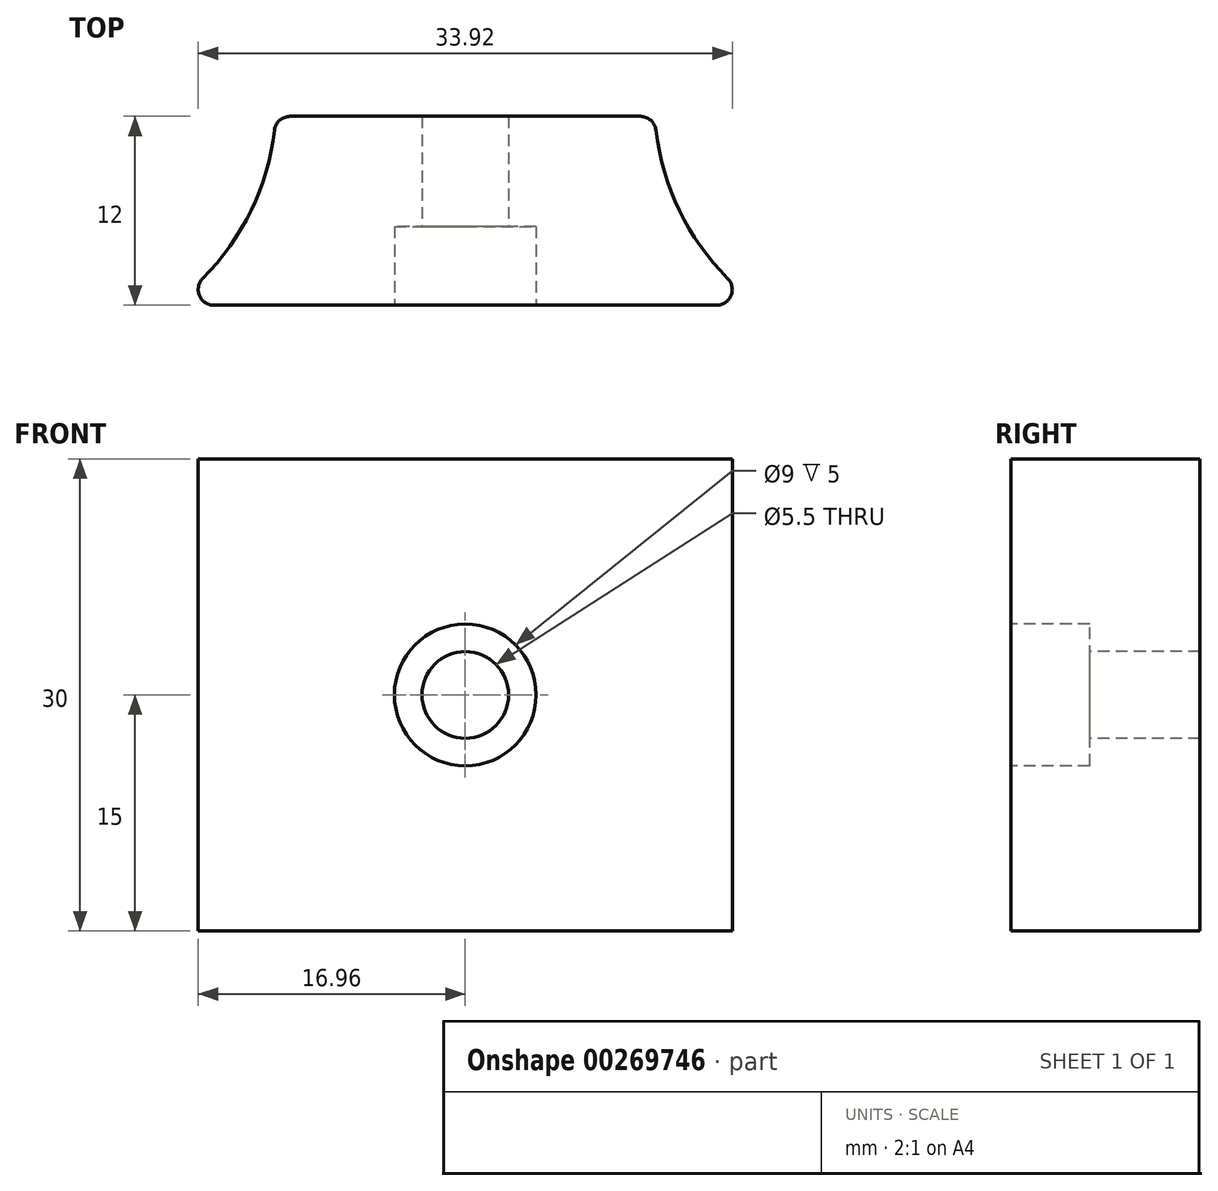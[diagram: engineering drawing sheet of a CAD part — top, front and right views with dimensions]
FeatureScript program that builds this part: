
annotation { "Feature Type Name" : "Feature", "Feature Type Description" : "" }
export const myFeature = defineFeature(function(context is Context, id is Id, definition is map)
    precondition{}
    {
        {
            var Q0;
            Q0=qCreatedBy(makeId("Top.planeOp"),FACE);
            var sketch = newSketch(context, id + "F0", { "sketchPlane" : qUnion([Q0])});
            skCircle(sketch, "E0", {"center": v(-28, 0) * mm, "radius": 16 * mm});
            skCircle(sketch, "E1", {"center": v(28, 0) * mm, "radius": 16 * mm});
            skLineSegment(sketch, "E2", {"start": v(-28, 0) * mm, "end": v(0, 0) * mm, "construction": true});
            skLineSegment(sketch, "E3", {"start": v(0, 0) * mm, "end": v(28, 0) * mm, "construction": true});
            skLineSegment(sketch, "E4", {"start": v(-12.03, -1) * mm, "end": v(12.03, -1) * mm});
            skLineSegment(sketch, "E5", {"start": v(-18.67, -13) * mm, "end": v(18.67, -13) * mm});
            skSolve(sketch);
        }
        {
            var Q0;
            {var subQ0=sQuery(id+"F0.wireOp",EDGE,"E4");Q0=makeQuery(id+"F0.imprint","IMPRINT",FACE,{"disambiguationData":[TD([[makeQuery(id+"F0.imprint","IMPRINT",EDGE,{"derivedFrom":subQ0}),-1.0]])]});}
            extrude(context, id + "F1", {"entities" : qUnion([Q0]), "depth" : 30 * mm});
        }
        {
            var Q0;
            Q0=makeQuery(id+"F1.opExtrude","SWEPT_FACE",FACE,{"disambiguationData":[OSD([sQuery(id+"F0.wireOp",EDGE,"E5")])]});
            var sketch = newSketch(context, id + "F2", { "sketchPlane" : qUnion([Q0])});
            skCircle(sketch, "E6", {"center": v(0, 15) * mm, "radius": 2.75 * mm});
            skCircle(sketch, "E7", {"center": v(0, 15) * mm, "radius": 4.5 * mm});
            skSolve(sketch);
        }
        {
            var Q0;
            Q0 = qSketchRegion(id + "F2", true);
            extrude(context, id + "F3", {"entities" : qUnion([Q0]), "operationType" : NewBodyOperationType.REMOVE, "oppositeDirection" : true, "depth" : 5 * mm});
        }
        {
            var Q0;
            Q0=makeQuery(id+"F3.boolean.opBoolean","SPLIT",FACE,{"disambiguationData":[TD([makeQuery(id+"F3.opExtrude","SWEPT_FACE",FACE,{"disambiguationData":[OSD([sQuery(id+"F2.wireOp",EDGE,"E6")])]})])],"derivedFrom":makeQuery(id+"F1.opExtrude","SWEPT_FACE",FACE,{"disambiguationData":[OSD([sQuery(id+"F0.wireOp",EDGE,"E5")])]})});
            extrude(context, id + "F4", {"entities" : qUnion([Q0]), "operationType" : NewBodyOperationType.REMOVE, "endBound" : BoundingType.UP_TO_NEXT, "oppositeDirection" : true, "depth" : 25 * mm});
        }
        {
            var Q0;
            Q0=makeQuery(id+"F1.opExtrude","SWEPT_EDGE",EDGE,{"disambiguationData":[OSD([sQuery(id+"F0.wireOp",EDGE,"E0"),sQuery(id+"F0.wireOp",EDGE,"E5")])]});
            var Q1;
            Q1=makeQuery(id+"F1.opExtrude","SWEPT_EDGE",EDGE,{"disambiguationData":[OSD([sQuery(id+"F0.wireOp",EDGE,"E0"),sQuery(id+"F0.wireOp",EDGE,"E4")])]});
            var Q2;
            Q2=makeQuery(id+"F1.opExtrude","SWEPT_EDGE",EDGE,{"disambiguationData":[OSD([sQuery(id+"F0.wireOp",EDGE,"E1"),sQuery(id+"F0.wireOp",EDGE,"E5")])]});
            var Q3;
            Q3=makeQuery(id+"F1.opExtrude","SWEPT_EDGE",EDGE,{"disambiguationData":[OSD([sQuery(id+"F0.wireOp",EDGE,"E1"),sQuery(id+"F0.wireOp",EDGE,"E4")])]});
            fillet(context, id + "F5", {"entities" : qUnion([Q0, Q1, Q2, Q3]), "radius" : 1 * mm, "tangentPropagation" : true, "allowEdgeOverflow" : false});
        }
    });
